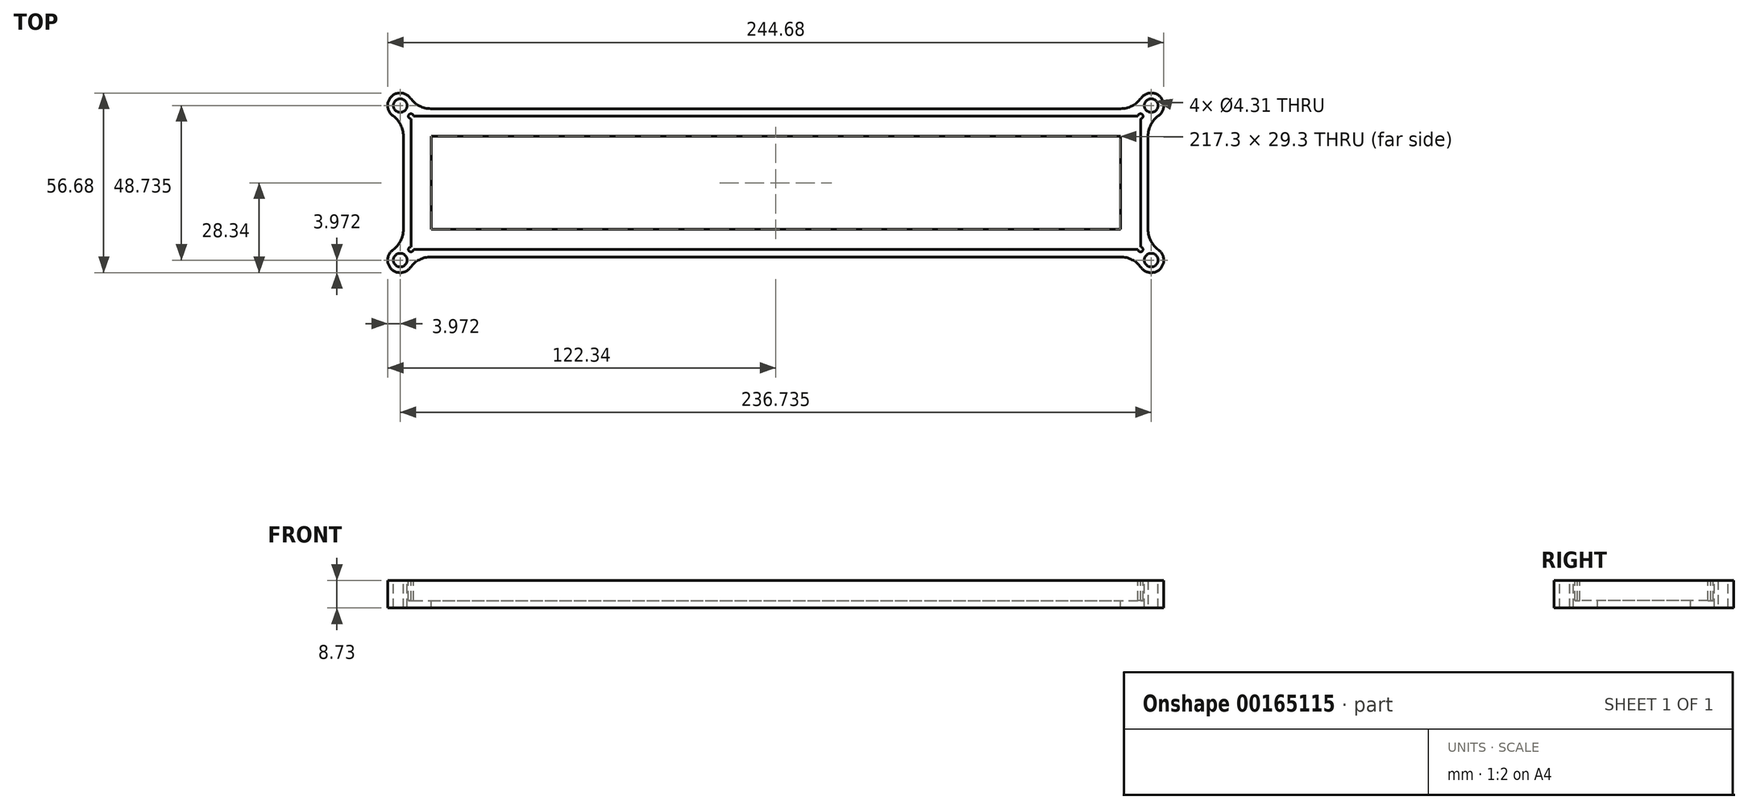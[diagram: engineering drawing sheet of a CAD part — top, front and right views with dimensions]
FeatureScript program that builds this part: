
annotation { "Feature Type Name" : "Feature", "Feature Type Description" : "" }
export const myFeature = defineFeature(function(context is Context, id is Id, definition is map)
    precondition{}
    {
        {
            var Q0;
            Q0=qCreatedBy(makeId("Top.planeOp"),FACE);
            var sketch = newSketch(context, id + "F0", { "sketchPlane" : qUnion([Q0])});
            skLineSegment(sketch, "E0.bottom", {"start": v(-115, 21) * mm, "end": v(115, 21) * mm});
            skLineSegment(sketch, "E0.top", {"start": v(-115, -21) * mm, "end": v(115, -21) * mm});
            skLineSegment(sketch, "E0.left", {"start": v(-115, 21) * mm, "end": v(-115, -21) * mm});
            skLineSegment(sketch, "E0.right", {"start": v(115, 21) * mm, "end": v(115, -21) * mm});
            skPoint(sketch, "E0.middle", {"position": v(0, 0) * mm});
            skLineSegment(sketch, "E1.bottom", {"start": v(-117.38, 23.38) * mm, "end": v(117.38, 23.38) * mm});
            skLineSegment(sketch, "E1.top", {"start": v(-117.38, -23.38) * mm, "end": v(117.38, -23.38) * mm});
            skLineSegment(sketch, "E1.left", {"start": v(-117.38, 23.38) * mm, "end": v(-117.38, -23.38) * mm});
            skLineSegment(sketch, "E1.right", {"start": v(117.38, 23.38) * mm, "end": v(117.38, -23.38) * mm});
            skLineSegment(sketch, "E2", {"start": v(-115, 21) * mm, "end": v(-117.38, 21) * mm, "construction": true});
            skLineSegment(sketch, "E3", {"start": v(-115, 21) * mm, "end": v(-115, 23.38) * mm, "construction": true});
            skSolve(sketch);
        }
        {
            var Q0;
            Q0=qSketchRegion(id+"F0",true);
            extrude(context, id + "F1", {"entities" : qUnion([Q0]), "depth" : 6.35 * mm});
        }
        {
            var Q0;
            Q0=makeQuery(id+"F1.opExtrude","CAP_FACE",FACE,{"disambiguationData":[OSD([sQuery(id+"F0.wireOp",EDGE,"E0.bottom"),sQuery(id+"F0.wireOp",EDGE,"E0.top"),sQuery(id+"F0.wireOp",EDGE,"E0.left"),sQuery(id+"F0.wireOp",EDGE,"E0.right"),sQuery(id+"F0.wireOp",EDGE,"E1.bottom"),sQuery(id+"F0.wireOp",EDGE,"E1.top"),sQuery(id+"F0.wireOp",EDGE,"E1.left"),sQuery(id+"F0.wireOp",EDGE,"E1.right")])],"isStart":true});
            var sketch = newSketch(context, id + "F2", { "sketchPlane" : qUnion([Q0])});
            skLineSegment(sketch, "E4.bottom", {"start": v(-117.38, 23.38) * mm, "end": v(117.38, 23.38) * mm});
            skLineSegment(sketch, "E4.top", {"start": v(-117.38, -23.38) * mm, "end": v(117.38, -23.38) * mm});
            skLineSegment(sketch, "E4.left", {"start": v(-117.38, 23.38) * mm, "end": v(-117.38, -23.38) * mm});
            skLineSegment(sketch, "E4.right", {"start": v(117.38, 23.38) * mm, "end": v(117.38, -23.38) * mm});
            skLineSegment(sketch, "E5", {"start": v(0, 21) * mm, "end": v(0, -21) * mm, "construction": true});
            skLineSegment(sketch, "E6.bottom", {"start": v(-108.65, -14.65) * mm, "end": v(108.65, -14.65) * mm});
            skLineSegment(sketch, "E6.top", {"start": v(-108.65, 14.65) * mm, "end": v(108.65, 14.65) * mm});
            skLineSegment(sketch, "E6.left", {"start": v(-108.65, -14.65) * mm, "end": v(-108.65, 14.65) * mm});
            skLineSegment(sketch, "E6.right", {"start": v(108.65, -14.65) * mm, "end": v(108.65, 14.65) * mm});
            skPoint(sketch, "E6.middle", {"position": v(0, 0) * mm});
            skLineSegment(sketch, "E7.bottom", {"start": v(-108.65, -14.65) * mm, "end": v(-115, -14.65) * mm, "construction": true});
            skLineSegment(sketch, "E7.top", {"start": v(-108.65, -21) * mm, "end": v(-115, -21) * mm, "construction": true});
            skLineSegment(sketch, "E7.left", {"start": v(-108.65, -14.65) * mm, "end": v(-108.65, -21) * mm, "construction": true});
            skLineSegment(sketch, "E7.right", {"start": v(-115, -14.65) * mm, "end": v(-115, -21) * mm, "construction": true});
            skSolve(sketch);
        }
        {
            var Q0;
            Q0=qSketchRegion(id+"F2",true);
            extrude(context, id + "F3", {"entities" : qUnion([Q0]), "operationType" : NewBodyOperationType.ADD, "depth" : 2.38 * mm});
        }
        {
            var Q0;
            Q0=makeQuery(id+"F1.opExtrude","CAP_FACE",FACE,{"disambiguationData":[OSD([sQuery(id+"F0.wireOp",EDGE,"E0.bottom"),sQuery(id+"F0.wireOp",EDGE,"E0.top"),sQuery(id+"F0.wireOp",EDGE,"E0.left"),sQuery(id+"F0.wireOp",EDGE,"E0.right"),sQuery(id+"F0.wireOp",EDGE,"E1.bottom"),sQuery(id+"F0.wireOp",EDGE,"E1.top"),sQuery(id+"F0.wireOp",EDGE,"E1.left"),sQuery(id+"F0.wireOp",EDGE,"E1.right")])],"isStart":false});
            var sketch = newSketch(context, id + "F4", { "sketchPlane" : qUnion([Q0])});
            skLineSegment(sketch, "E8.bottom", {"start": v(117.38, 23.38) * mm, "end": v(118.37, 23.38) * mm, "construction": true});
            skLineSegment(sketch, "E8.top", {"start": v(117.38, 24.37) * mm, "end": v(118.37, 24.37) * mm, "construction": true});
            skLineSegment(sketch, "E8.left", {"start": v(117.38, 23.38) * mm, "end": v(117.38, 24.37) * mm, "construction": true});
            skLineSegment(sketch, "E8.right", {"start": v(118.37, 23.38) * mm, "end": v(118.37, 24.37) * mm, "construction": true});
            skLineSegment(sketch, "E9", {"start": v(0, 23.38) * mm, "end": v(0, -23.38) * mm, "construction": true});
            skLineSegment(sketch, "E10.bottom", {"start": v(118.37, 24.37) * mm, "end": v(-118.37, 24.37) * mm, "construction": true});
            skLineSegment(sketch, "E10.top", {"start": v(118.37, -24.37) * mm, "end": v(-118.37, -24.37) * mm, "construction": true});
            skLineSegment(sketch, "E10.left", {"start": v(118.37, 24.37) * mm, "end": v(118.37, -24.37) * mm, "construction": true});
            skLineSegment(sketch, "E10.right", {"start": v(-118.37, 24.37) * mm, "end": v(-118.37, -24.37) * mm, "construction": true});
            skPoint(sketch, "E10.middle", {"position": v(0, 0) * mm});
            skCircle(sketch, "E11", {"center": v(118.37, 24.37) * mm, "radius": 3.97 * mm});
            skCircle(sketch, "E12", {"center": v(118.37, -24.37) * mm, "radius": 3.97 * mm});
            skCircle(sketch, "E13", {"center": v(-118.37, -24.37) * mm, "radius": 3.97 * mm});
            skCircle(sketch, "E14", {"center": v(-118.37, 24.37) * mm, "radius": 3.97 * mm});
            skCircle(sketch, "E15", {"center": v(115, 21) * mm, "radius": 0.8 * mm, "construction": true});
            skSolve(sketch);
        }
        {
            var Q0;
            Q0=qSketchRegion(id+"F4",true);
            var Q1;
            Q1=makeQuery(id+"F3.opExtrude","CAP_FACE",FACE,{"disambiguationData":[OSD([sQuery(id+"F2.wireOp",EDGE,"E4.bottom"),sQuery(id+"F2.wireOp",EDGE,"E4.top"),sQuery(id+"F2.wireOp",EDGE,"E4.left"),sQuery(id+"F2.wireOp",EDGE,"E4.right")])],"isStart":false});
            extrude(context, id + "F5", {"entities" : qUnion([Q0]), "operationType" : NewBodyOperationType.ADD, "endBound" : BoundingType.UP_TO_SURFACE, "oppositeDirection" : true, "endBoundEntityFace" : qUnion([Q1]), "depth" : 25.4 * mm});
        }
        {
            var Q0;
            Q0=makeQuery(id+"F5.boolean.opBoolean","INTERSECT",EDGE,{"derivedFrom":[makeQuery(id+"F3.boolean.opBoolean","MERGE",FACE,{"derivedFrom":[makeQuery(id+"F1.opExtrude","SWEPT_FACE",FACE,{"disambiguationData":[OSD([sQuery(id+"F0.wireOp",EDGE,"E1.bottom")])]}),makeQuery(id+"F3.opExtrude","SWEPT_FACE",FACE,{"disambiguationData":[OSD([sQuery(id+"F2.wireOp",EDGE,"E4.top")])]})]}),makeQuery(id+"F5.opExtrude","SWEPT_FACE",FACE,{"disambiguationData":[OSD([sQuery(id+"F4.wireOp",EDGE,"E11")])]})]});
            var Q1;
            Q1=makeQuery(id+"F5.boolean.opBoolean","INTERSECT",EDGE,{"derivedFrom":[makeQuery(id+"F3.boolean.opBoolean","MERGE",FACE,{"derivedFrom":[makeQuery(id+"F1.opExtrude","SWEPT_FACE",FACE,{"disambiguationData":[OSD([sQuery(id+"F0.wireOp",EDGE,"E1.right")])]}),makeQuery(id+"F3.opExtrude","SWEPT_FACE",FACE,{"disambiguationData":[OSD([sQuery(id+"F2.wireOp",EDGE,"E4.right")])]})]}),makeQuery(id+"F5.opExtrude","SWEPT_FACE",FACE,{"disambiguationData":[OSD([sQuery(id+"F4.wireOp",EDGE,"E11")])]})]});
            var Q2;
            Q2=makeQuery(id+"F5.boolean.opBoolean","INTERSECT",EDGE,{"derivedFrom":[makeQuery(id+"F3.boolean.opBoolean","MERGE",FACE,{"derivedFrom":[makeQuery(id+"F1.opExtrude","SWEPT_FACE",FACE,{"disambiguationData":[OSD([sQuery(id+"F0.wireOp",EDGE,"E1.right")])]}),makeQuery(id+"F3.opExtrude","SWEPT_FACE",FACE,{"disambiguationData":[OSD([sQuery(id+"F2.wireOp",EDGE,"E4.right")])]})]}),makeQuery(id+"F5.opExtrude","SWEPT_FACE",FACE,{"disambiguationData":[OSD([sQuery(id+"F4.wireOp",EDGE,"E12")])]})]});
            var Q3;
            Q3=makeQuery(id+"F5.boolean.opBoolean","INTERSECT",EDGE,{"derivedFrom":[makeQuery(id+"F3.boolean.opBoolean","MERGE",FACE,{"derivedFrom":[makeQuery(id+"F1.opExtrude","SWEPT_FACE",FACE,{"disambiguationData":[OSD([sQuery(id+"F0.wireOp",EDGE,"E1.top")])]}),makeQuery(id+"F3.opExtrude","SWEPT_FACE",FACE,{"disambiguationData":[OSD([sQuery(id+"F2.wireOp",EDGE,"E4.bottom")])]})]}),makeQuery(id+"F5.opExtrude","SWEPT_FACE",FACE,{"disambiguationData":[OSD([sQuery(id+"F4.wireOp",EDGE,"E12")])]})]});
            var Q4;
            Q4=makeQuery(id+"F5.boolean.opBoolean","INTERSECT",EDGE,{"derivedFrom":[makeQuery(id+"F3.boolean.opBoolean","MERGE",FACE,{"derivedFrom":[makeQuery(id+"F1.opExtrude","SWEPT_FACE",FACE,{"disambiguationData":[OSD([sQuery(id+"F0.wireOp",EDGE,"E1.left")])]}),makeQuery(id+"F3.opExtrude","SWEPT_FACE",FACE,{"disambiguationData":[OSD([sQuery(id+"F2.wireOp",EDGE,"E4.left")])]})]}),makeQuery(id+"F5.opExtrude","SWEPT_FACE",FACE,{"disambiguationData":[OSD([sQuery(id+"F4.wireOp",EDGE,"E13")])]})]});
            var Q5;
            Q5=makeQuery(id+"F5.boolean.opBoolean","INTERSECT",EDGE,{"derivedFrom":[makeQuery(id+"F3.boolean.opBoolean","MERGE",FACE,{"derivedFrom":[makeQuery(id+"F1.opExtrude","SWEPT_FACE",FACE,{"disambiguationData":[OSD([sQuery(id+"F0.wireOp",EDGE,"E1.top")])]}),makeQuery(id+"F3.opExtrude","SWEPT_FACE",FACE,{"disambiguationData":[OSD([sQuery(id+"F2.wireOp",EDGE,"E4.bottom")])]})]}),makeQuery(id+"F5.opExtrude","SWEPT_FACE",FACE,{"disambiguationData":[OSD([sQuery(id+"F4.wireOp",EDGE,"E13")])]})]});
            var Q6;
            Q6=makeQuery(id+"F5.boolean.opBoolean","INTERSECT",EDGE,{"derivedFrom":[makeQuery(id+"F3.boolean.opBoolean","MERGE",FACE,{"derivedFrom":[makeQuery(id+"F1.opExtrude","SWEPT_FACE",FACE,{"disambiguationData":[OSD([sQuery(id+"F0.wireOp",EDGE,"E1.bottom")])]}),makeQuery(id+"F3.opExtrude","SWEPT_FACE",FACE,{"disambiguationData":[OSD([sQuery(id+"F2.wireOp",EDGE,"E4.top")])]})]}),makeQuery(id+"F5.opExtrude","SWEPT_FACE",FACE,{"disambiguationData":[OSD([sQuery(id+"F4.wireOp",EDGE,"E14")])]})]});
            var Q7;
            Q7=makeQuery(id+"F5.boolean.opBoolean","INTERSECT",EDGE,{"derivedFrom":[makeQuery(id+"F3.boolean.opBoolean","MERGE",FACE,{"derivedFrom":[makeQuery(id+"F1.opExtrude","SWEPT_FACE",FACE,{"disambiguationData":[OSD([sQuery(id+"F0.wireOp",EDGE,"E1.left")])]}),makeQuery(id+"F3.opExtrude","SWEPT_FACE",FACE,{"disambiguationData":[OSD([sQuery(id+"F2.wireOp",EDGE,"E4.left")])]})]}),makeQuery(id+"F5.opExtrude","SWEPT_FACE",FACE,{"disambiguationData":[OSD([sQuery(id+"F4.wireOp",EDGE,"E14")])]})]});
            fillet(context, id + "F6", {"entities" : qUnion([Q0, Q1, Q2, Q3, Q4, Q5, Q6, Q7]), "radius" : 7.94 * mm, "tangentPropagation" : true, "allowEdgeOverflow" : false});
        }
        {
            var Q0;
            Q0=makeQuery(id+"F5.boolean.opBoolean","MERGE",FACE,{"derivedFrom":[makeQuery(id+"F1.opExtrude","CAP_FACE",FACE,{"disambiguationData":[OSD([sQuery(id+"F0.wireOp",EDGE,"E0.bottom"),sQuery(id+"F0.wireOp",EDGE,"E0.top"),sQuery(id+"F0.wireOp",EDGE,"E0.left"),sQuery(id+"F0.wireOp",EDGE,"E0.right"),sQuery(id+"F0.wireOp",EDGE,"E1.bottom"),sQuery(id+"F0.wireOp",EDGE,"E1.top"),sQuery(id+"F0.wireOp",EDGE,"E1.left"),sQuery(id+"F0.wireOp",EDGE,"E1.right")])],"isStart":false}),makeQuery(id+"F5.opExtrude","CAP_FACE",FACE,{"disambiguationData":[OSD([sQuery(id+"F4.wireOp",EDGE,"E11")])],"isStart":true}),makeQuery(id+"F5.opExtrude","CAP_FACE",FACE,{"disambiguationData":[OSD([sQuery(id+"F4.wireOp",EDGE,"E12")])],"isStart":true}),makeQuery(id+"F5.opExtrude","CAP_FACE",FACE,{"disambiguationData":[OSD([sQuery(id+"F4.wireOp",EDGE,"E13")])],"isStart":true}),makeQuery(id+"F5.opExtrude","CAP_FACE",FACE,{"disambiguationData":[OSD([sQuery(id+"F4.wireOp",EDGE,"E14")])],"isStart":true})]});
            var sketch = newSketch(context, id + "F7", { "sketchPlane" : qUnion([Q0])});
            skCircle(sketch, "E16", {"center": v(118.37, 24.37) * mm, "radius": 2.15 * mm});
            skCircle(sketch, "E17", {"center": v(118.37, -24.37) * mm, "radius": 2.15 * mm});
            skCircle(sketch, "E18", {"center": v(-118.37, 24.37) * mm, "radius": 2.15 * mm});
            skCircle(sketch, "E19", {"center": v(-118.37, -24.37) * mm, "radius": 2.15 * mm});
            skSolve(sketch);
        }
        {
            var Q0;
            Q0=qSketchRegion(id+"F7",true);
            var Q1;
            Q1=makeQuery(id+"F5.boolean.opBoolean","MERGE",FACE,{"derivedFrom":[makeQuery(id+"F3.opExtrude","CAP_FACE",FACE,{"disambiguationData":[OSD([sQuery(id+"F2.wireOp",EDGE,"E4.bottom"),sQuery(id+"F2.wireOp",EDGE,"E4.top"),sQuery(id+"F2.wireOp",EDGE,"E4.left"),sQuery(id+"F2.wireOp",EDGE,"E4.right"),sQuery(id+"F2.wireOp",EDGE,"E6.bottom"),sQuery(id+"F2.wireOp",EDGE,"E6.top"),sQuery(id+"F2.wireOp",EDGE,"E6.left"),sQuery(id+"F2.wireOp",EDGE,"E6.right")])],"isStart":false}),makeQuery(id+"F5.opExtrude","CAP_FACE",FACE,{"disambiguationData":[OSD([sQuery(id+"F4.wireOp",EDGE,"E11")])],"isStart":false}),makeQuery(id+"F5.opExtrude","CAP_FACE",FACE,{"disambiguationData":[OSD([sQuery(id+"F4.wireOp",EDGE,"E12")])],"isStart":false}),makeQuery(id+"F5.opExtrude","CAP_FACE",FACE,{"disambiguationData":[OSD([sQuery(id+"F4.wireOp",EDGE,"E13")])],"isStart":false}),makeQuery(id+"F5.opExtrude","CAP_FACE",FACE,{"disambiguationData":[OSD([sQuery(id+"F4.wireOp",EDGE,"E14")])],"isStart":false})]});
            extrude(context, id + "F8", {"entities" : qUnion([Q0]), "operationType" : NewBodyOperationType.REMOVE, "endBound" : BoundingType.UP_TO_SURFACE, "oppositeDirection" : true, "endBoundEntityFace" : qUnion([Q1]), "depth" : 25.4 * mm});
        }
        {
            var Q0;
            Q0=makeQuery(id+"F5.boolean.opBoolean","MERGE",FACE,{"derivedFrom":[makeQuery(id+"F1.opExtrude","CAP_FACE",FACE,{"disambiguationData":[OSD([sQuery(id+"F0.wireOp",EDGE,"E0.bottom"),sQuery(id+"F0.wireOp",EDGE,"E0.top"),sQuery(id+"F0.wireOp",EDGE,"E0.left"),sQuery(id+"F0.wireOp",EDGE,"E0.right"),sQuery(id+"F0.wireOp",EDGE,"E1.bottom"),sQuery(id+"F0.wireOp",EDGE,"E1.top"),sQuery(id+"F0.wireOp",EDGE,"E1.left"),sQuery(id+"F0.wireOp",EDGE,"E1.right")])],"isStart":false}),makeQuery(id+"F5.opExtrude","CAP_FACE",FACE,{"disambiguationData":[OSD([sQuery(id+"F4.wireOp",EDGE,"E11")])],"isStart":true}),makeQuery(id+"F5.opExtrude","CAP_FACE",FACE,{"disambiguationData":[OSD([sQuery(id+"F4.wireOp",EDGE,"E12")])],"isStart":true}),makeQuery(id+"F5.opExtrude","CAP_FACE",FACE,{"disambiguationData":[OSD([sQuery(id+"F4.wireOp",EDGE,"E13")])],"isStart":true}),makeQuery(id+"F5.opExtrude","CAP_FACE",FACE,{"disambiguationData":[OSD([sQuery(id+"F4.wireOp",EDGE,"E14")])],"isStart":true})]});
            var sketch = newSketch(context, id + "F9", { "sketchPlane" : qUnion([Q0])});
            skCircle(sketch, "E20", {"center": v(-115, 21) * mm, "radius": 0.8 * mm});
            skCircle(sketch, "E21", {"center": v(-115, -21) * mm, "radius": 0.8 * mm});
            skCircle(sketch, "E22", {"center": v(115, 21) * mm, "radius": 0.8 * mm});
            skCircle(sketch, "E23", {"center": v(115, -21) * mm, "radius": 0.8 * mm});
            skSolve(sketch);
        }
        {
            var Q0;
            Q0 = qSketchRegion(id + "F9", true);
            var Q1;
            Q1=makeQuery(id+"F3.opExtrude","CAP_FACE",FACE,{"disambiguationData":[OSD([sQuery(id+"F2.wireOp",EDGE,"E4.bottom"),sQuery(id+"F2.wireOp",EDGE,"E4.top"),sQuery(id+"F2.wireOp",EDGE,"E4.left"),sQuery(id+"F2.wireOp",EDGE,"E4.right")])],"isStart":true});
            extrude(context, id + "F10", {"entities" : qUnion([Q0]), "operationType" : NewBodyOperationType.REMOVE, "endBound" : BoundingType.UP_TO_SURFACE, "oppositeDirection" : true, "endBoundEntityFace" : qUnion([Q1]), "depth" : 25.4 * mm});
        }
    });
